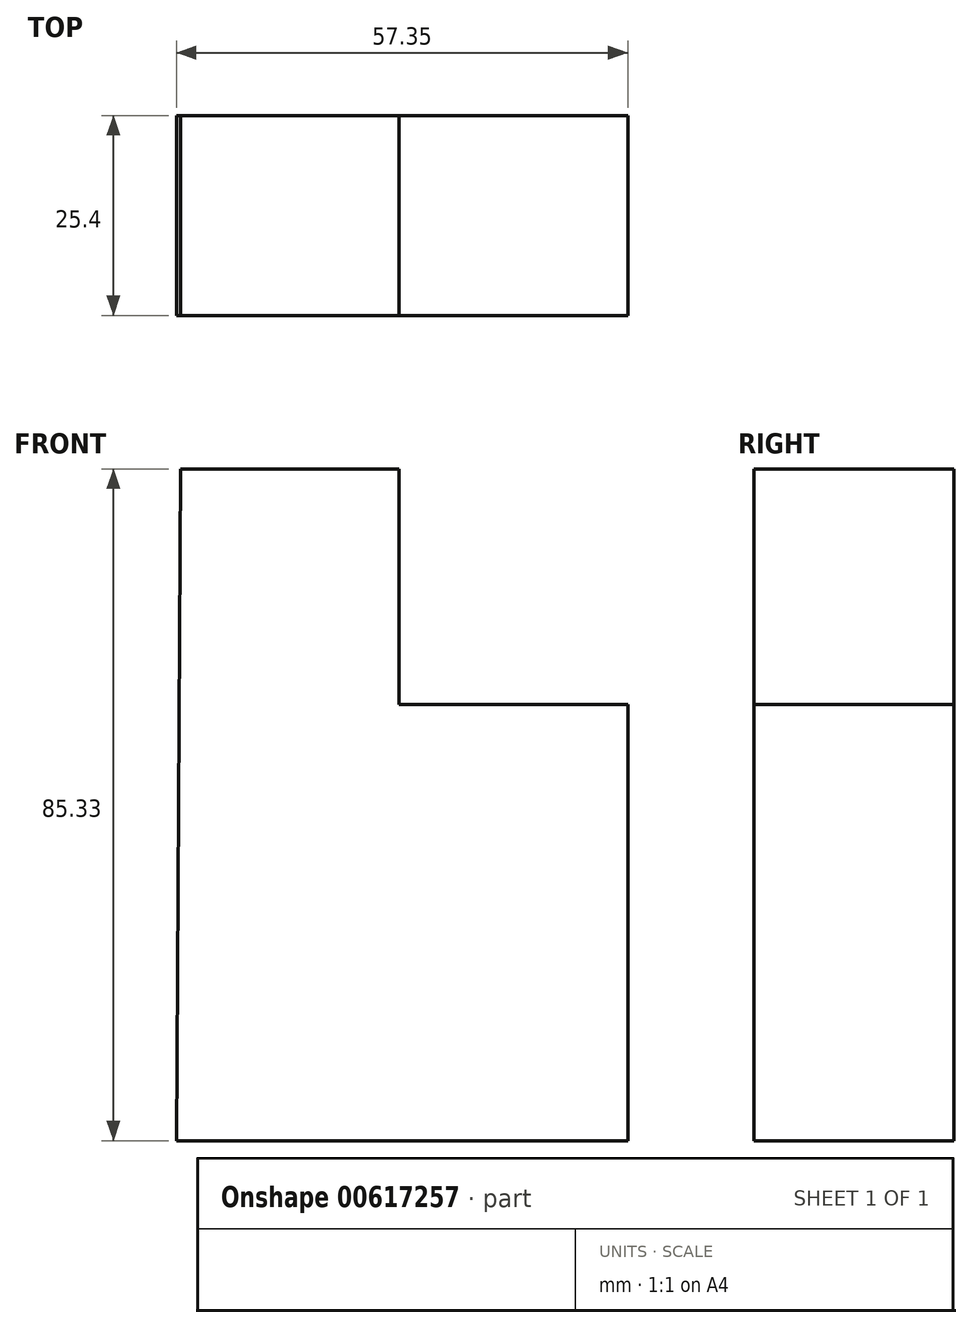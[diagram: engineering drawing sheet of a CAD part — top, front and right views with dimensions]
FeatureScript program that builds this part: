
annotation { "Feature Type Name" : "Feature", "Feature Type Description" : "" }
export const myFeature = defineFeature(function(context is Context, id is Id, definition is map)
    precondition{}
    {
        {
            var Q0;
            Q0=qCreatedBy(makeId("Front.planeOp"),FACE);
            var sketch = newSketch(context, id + "F0", { "sketchPlane" : qUnion([Q0])});
            skLineSegment(sketch, "E0", {"start": v(-53.85, 47.98) * mm, "end": v(-26.16, 47.98) * mm});
            skLineSegment(sketch, "E1", {"start": v(-26.16, 47.98) * mm, "end": v(-26.16, 18.04) * mm});
            skLineSegment(sketch, "E2", {"start": v(-26.16, 18.04) * mm, "end": v(2.94, 18.04) * mm});
            skLineSegment(sketch, "E3", {"start": v(2.94, 18.04) * mm, "end": v(2.94, -37.35) * mm});
            skLineSegment(sketch, "E4", {"start": v(2.94, -37.35) * mm, "end": v(-54.41, -37.35) * mm});
            skLineSegment(sketch, "E5", {"start": v(-53.85, 47.98) * mm, "end": v(-54.41, -37.35) * mm});
            skSolve(sketch);
        }
        {
            var Q0;
            Q0 = qSketchRegion(id + "F0", true);
            extrude(context, id + "F1", {"entities" : qUnion([Q0]), "depth" : 25.4 * mm, "offsetDistance" : 25.4 * mm});
        }
    });
